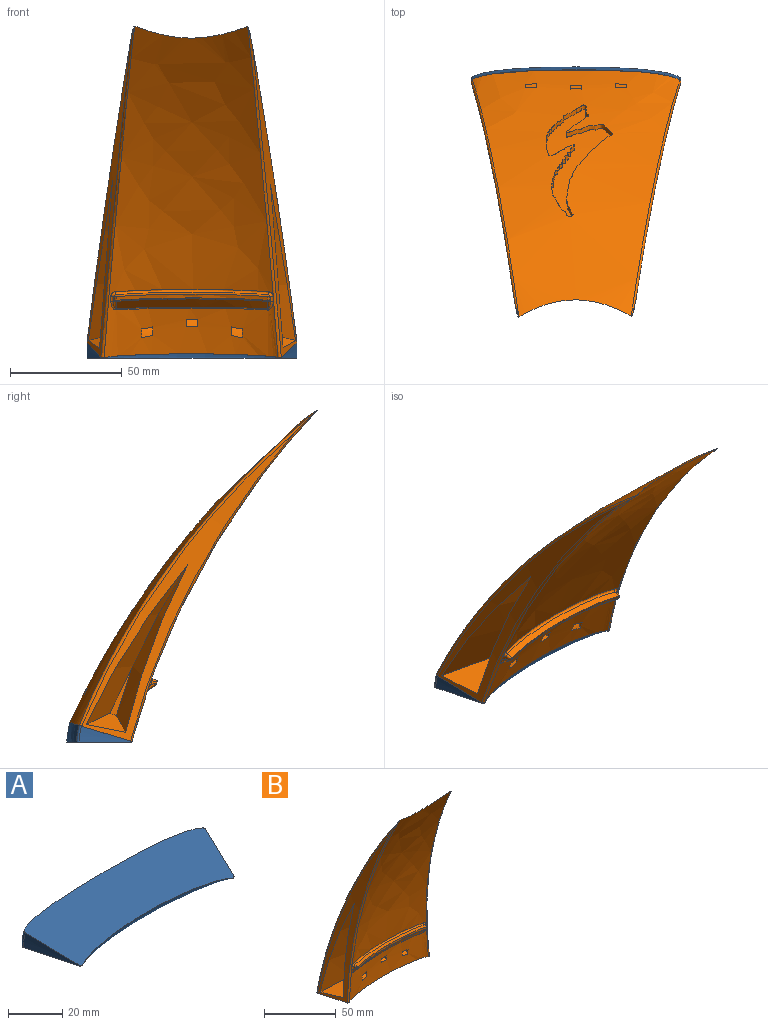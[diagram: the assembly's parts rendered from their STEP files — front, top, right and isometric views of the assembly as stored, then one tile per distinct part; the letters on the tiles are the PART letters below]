
ASSEMBLY  parts=2 mates=1
PART A: 10 faces, bbox 94x30.1x9 mm
  f0: cone r=1.44mm half-angle=72.8deg, axis (1,0,0), area 89.4mm2, adj f1,f7,f8,f9
  f1: torus R=24.33mm, axis (-1,0,0), area 9.8mm2, adj f0,f2,f8,f9
  f2: revolved ~93.01x8.73mm, area 804.6mm2, adj f1,f3,f8,f9
  f3: torus R=24.54mm, axis (-1,0,0), area 9.8mm2, adj f2,f4,f8,f9
  f4: cone r=1.4mm half-angle=75deg, axis (-1,0,0), area 90.3mm2, adj f3,f5,f8,f9
  f5: torus R=1.66mm, axis (-1,0,0), area 0.5mm2, adj f4,f6,f8,f9
  f6: revolved ~77.85x5.74mm, area 115mm2, adj f5,f7,f8,f9
  f7: torus R=1.73mm, axis (-1,0,0), area 0.5mm2, adj f0,f6,f8,f9
  f8: plane 94.01x28.74mm, normal (0,-0.29,0.96), area 2154.1mm2, adj f0,f1,f2,f3,f4,f5,f6,f7
  f9: plane 94.01x30.05mm, normal (0,0,-1), area 2154.1mm2, adj f0,f1,f2,f3,f4,f5,f6,f7
PART B: 53 faces, bbox 100.8x76.6x179.4 mm
  f0: cone r=362.94mm half-angle=72.8deg, axis (1,0,0.08), area 1166.9mm2, adj f3,f4,f5,f45,f46,f47
  f1: bspline ~171.13x77.85mm, area 10212.8mm2, adj f2,f3,f4,f5,f6,f8,f9,f10
  f2: bspline ~175.83x93.01mm, area 11373.5mm2, adj f1,f3,f5,f6,f9,f10,f11,f12
  f3: plane 94.06x29.29mm, normal (0,0,-1), area 2153.2mm2, adj f0,f1,f2,f4,f5,f6,f7,f8
  f4: bspline ~169.81x38.35mm, area 258.5mm2, adj f0,f1,f3,f5
  f5: bspline ~172.13x65.23mm, area 289.3mm2, adj f0,f1,f2,f3,f4
  f6: bspline ~172.57x65.67mm, area 284.1mm2, adj f1,f2,f3,f7,f8
  f7: cone r=385.79mm half-angle=75deg, axis (-1,0,0.08), area 1151.1mm2, adj f3,f6,f8,f49,f50,f51
  f8: bspline ~176.59x42.01mm, area 265mm2, adj f1,f3,f6,f7
  f9: plane 22.05x9.69mm, normal (1,0,0), area 60.1mm2, adj f1,f2,f10,f12
  f10: cylinder r=16mm len=22.5mm, axis (1,0,0), area 126.2mm2, adj f1,f2,f9,f11
  f11: plane 22.36x10.61mm, normal (-1,0,0), area 61.7mm2, adj f1,f2,f10,f12
  f12: cylinder r=18.5mm len=22.04mm, axis (1,0,0), area 118.2mm2, adj f1,f2,f9,f11
  f13: plane 21.17x7.66mm, normal (1,0,0), area 55.6mm2, adj f1,f2,f14,f16
  f14: cylinder r=18mm len=21.04mm, axis (1,0,0), area 113.7mm2, adj f1,f2,f13,f15
  f15: plane 21.17x7.66mm, normal (-1,0,0), area 55.7mm2, adj f1,f2,f14,f16
  f16: cylinder r=20.5mm len=20.61mm, axis (1,0,0), area 109mm2, adj f1,f2,f13,f15
  f17: plane 22.34x10.55mm, normal (1,0,0), area 61.6mm2, adj f1,f2,f18,f20
  f18: cylinder r=16mm len=22.47mm, axis (1,0,0), area 126mm2, adj f1,f2,f17,f19
  f19: plane 22.03x9.65mm, normal (-1,0,0), area 60mm2, adj f1,f2,f18,f20
  f20: cylinder r=18.5mm len=22.01mm, axis (1,0,0), area 118.1mm2, adj f1,f2,f17,f19
  f21: bspline ~174.01x93.01mm, area 932.7mm2, adj f22
  f22: extruded ~78.95x29.94mm, area 408.4mm2, adj f2,f21
  f23: plane 2.42x1.47mm, normal (-1,0,0), area 2mm2, adj f31,f32,f40,f41
  f24: plane 2.3x1.38mm, normal (1,0,0), area 1.8mm2, adj f28,f29,f38,f39
  f25: bspline ~171.13x77.85mm, area 121.8mm2, adj f26,f28,f32,f33
  f26: plane 68.02x6.65mm, normal (0,0,1), area 197.6mm2, adj f25,f28,f29,f30,f31,f32
  f27: bspline ~73.47x8.86mm, area 416.7mm2, adj f33,f38,f41,f44
  f28: bspline ~37.95x4.91mm, area 2.7mm2, adj f24,f25,f26,f29,f34
  f29: cylinder r=1mm len=2.83mm, axis (0,1,0), area 3.2mm2, adj f24,f26,f28,f35
  f30: bspline ~69.81x5.03mm, area 114.1mm2, adj f1,f26,f35,f36
  f31: cylinder r=1mm len=2.84mm, axis (0,-1,0), area 3.2mm2, adj f23,f26,f32,f36
  f32: bspline ~35.13x4.75mm, area 2.7mm2, adj f23,f25,f26,f31,f37
  f33: bspline ~71.11x4.47mm, area 40.7mm2, adj f25,f27,f34,f37
  f34: sphere r=1mm, area 0.8mm2, adj f28,f33,f38
  f35: bspline ~2.61x2.38mm, area 4mm2, adj f1,f29,f30,f39
  f36: bspline ~2.44x2.14mm, area 3.9mm2, adj f1,f30,f31,f40
  f37: sphere r=1mm, area 0.5mm2, adj f32,f33,f41
  f38: bspline ~6.73x5.89mm, area 7.4mm2, adj f24,f27,f34,f42
  f39: bspline ~25.9x4.16mm, area 4.5mm2, adj f1,f24,f35,f42
  f40: bspline ~19.1x3.22mm, area 4.6mm2, adj f1,f23,f36,f43
  f41: bspline ~6.73x5.86mm, area 7.5mm2, adj f23,f27,f37,f43
  f42: bspline ~4.8x2.73mm, area 6.3mm2, adj f1,f38,f39,f44
  f43: bspline ~4.77x2.55mm, area 6mm2, adj f1,f40,f41,f44
  f44: bspline ~69.36x4.31mm, area 42mm2, adj f1,f27,f42,f43
  f45: plane 21.42x17.65mm, normal (0.34,0,0.94), area 200.7mm2, adj f0,f46,f47,f48
  f46: bspline ~85.05x30mm, area 1019.6mm2, adj f0,f45,f47,f48
  f47: bspline ~101.3x30mm, area 759.9mm2, adj f0,f45,f46,f48
  f48: plane 23.96x4.37mm, normal (1,0,0), area 38.2mm2, adj f45,f46,f47
  f49: plane 21.44x17.92mm, normal (-0.34,0,0.94), area 208.2mm2, adj f7,f50,f51,f52
  f50: bspline ~101.3x30mm, area 812mm2, adj f7,f49,f51,f52
  f51: bspline ~88.5x30.25mm, area 1050.7mm2, adj f7,f49,f50,f52
  f52: plane 23.96x4.37mm, normal (-1,0,0), area 38.2mm2, adj f49,f50,f51
PLACE A t=(-112.45,-61.49,4.77)mm
PLACE B rot(axis=(1,0,0),17deg) t=(-112.23,-51.27,12.04)mm
MATE planar B.f3 <-> A.f8  axis (0,0.29,-0.96) through (-112.44,-58.76,9.75)mm
